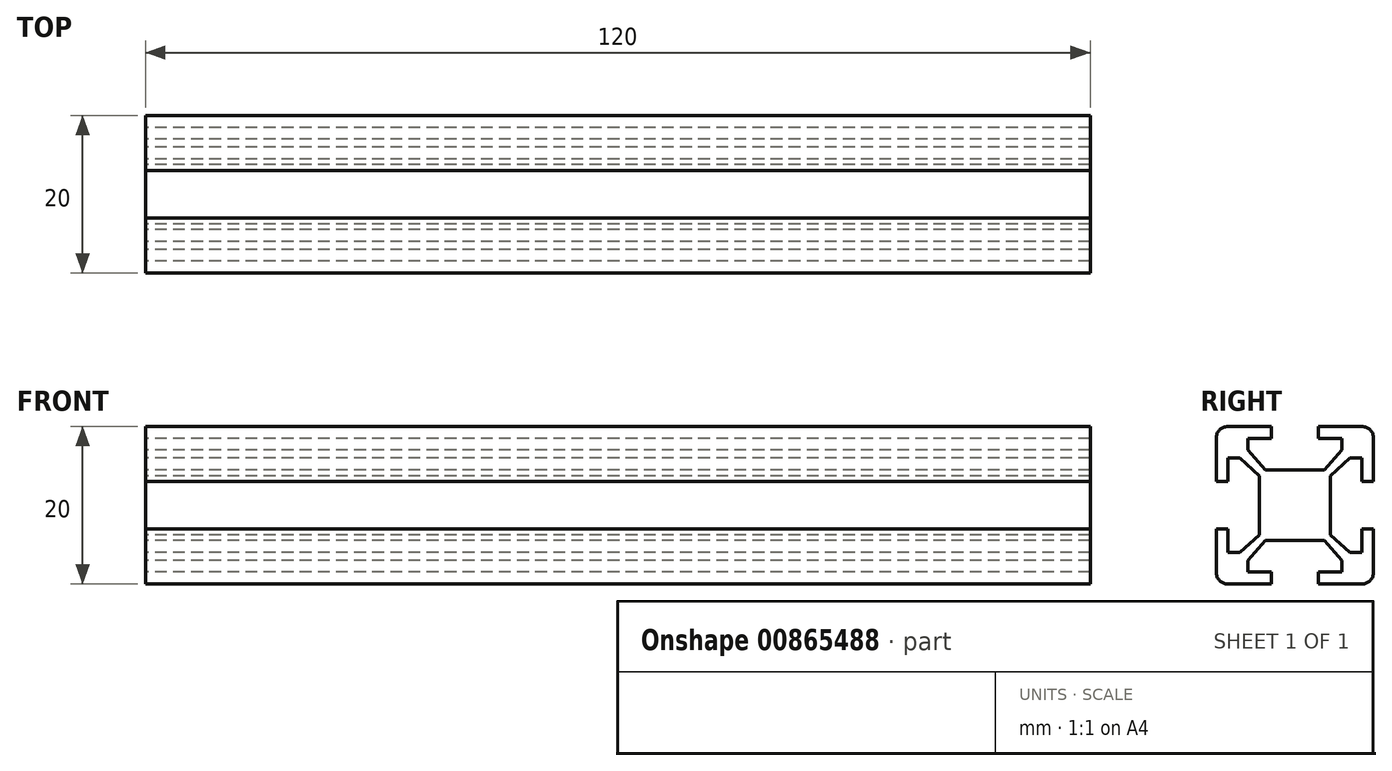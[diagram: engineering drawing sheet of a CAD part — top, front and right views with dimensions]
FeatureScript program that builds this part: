
annotation { "Feature Type Name" : "Feature", "Feature Type Description" : "" }
export const myFeature = defineFeature(function(context is Context, id is Id, definition is map)
    precondition{}
    {
        {
            var Q0;
            Q0=qCreatedBy(makeId("Right.planeOp"),FACE);
            var sketch = newSketch(context, id + "F0", { "sketchPlane" : qUnion([Q0])});
            skLineSegment(sketch, "E0.bottom", {"start": v(8.5, 10) * mm, "end": v(3, 10) * mm});
            skLineSegment(sketch, "E0.top", {"start": v(8.5, -10) * mm, "end": v(-8.5, -10) * mm});
            skLineSegment(sketch, "E0.left", {"start": v(10, 8.5) * mm, "end": v(10, 3) * mm});
            skLineSegment(sketch, "E0.right", {"start": v(-10, 8.5) * mm, "end": v(-10, 3) * mm});
            skPoint(sketch, "E0.middle", {"position": v(0, 0) * mm});
            skPoint(sketch, "E1.visualSharp", {"position": v(-10, 10) * mm});
            skArc(sketch, "E1.filletArc", {"start": v(-8.5, 10) * mm, "mid": v(-9.56, 9.56) * mm, "end": v(-10, 8.5) * mm});
            skPoint(sketch, "E2.visualSharp", {"position": v(10, 10) * mm});
            skArc(sketch, "E2.filletArc", {"start": v(10, 8.5) * mm, "mid": v(9.56, 9.56) * mm, "end": v(8.5, 10) * mm});
            skPoint(sketch, "E3.visualSharp", {"position": v(10, -10) * mm});
            skArc(sketch, "E3.filletArc", {"start": v(8.5, -10) * mm, "mid": v(9.56, -9.56) * mm, "end": v(10, -8.5) * mm});
            skPoint(sketch, "E4.visualSharp", {"position": v(-10, -10) * mm});
            skArc(sketch, "E4.filletArc", {"start": v(-10, -8.5) * mm, "mid": v(-9.56, -9.56) * mm, "end": v(-8.5, -10) * mm});
            skLineSegment(sketch, "E5", {"start": v(-3, 10) * mm, "end": v(-3, 8.5) * mm});
            skLineSegment(sketch, "E6", {"start": v(-3, 8.5) * mm, "end": v(-6, 8.5) * mm});
            skLineSegment(sketch, "E7", {"start": v(-6, 8.5) * mm, "end": v(-6, 7) * mm});
            skLineSegment(sketch, "E8", {"start": v(-6, 7) * mm, "end": v(-3.75, 4.5) * mm});
            skLineSegment(sketch, "E9", {"start": v(-3.75, 4.5) * mm, "end": v(0, 4.5) * mm});
            skLineSegment(sketch, "E10.MirrorCS", {"start": v(3, 10) * mm, "end": v(3, 8.5) * mm});
            skLineSegment(sketch, "E11.MirrorCS", {"start": v(3, 8.5) * mm, "end": v(6, 8.5) * mm});
            skLineSegment(sketch, "E12.MirrorCS", {"start": v(6, 8.5) * mm, "end": v(6, 7) * mm});
            skLineSegment(sketch, "E13.MirrorCS", {"start": v(6, 7) * mm, "end": v(3.75, 4.5) * mm});
            skLineSegment(sketch, "E14.MirrorCS", {"start": v(3.75, 4.5) * mm, "end": v(0, 4.5) * mm});
            skLineSegment(sketch, "E15.trimOffspring", {"start": v(-3, 10) * mm, "end": v(-8.5, 10) * mm});
            skLineSegment(sketch, "E16.1.0", {"start": v(-8.5, -3) * mm, "end": v(-8.5, -6) * mm});
            skLineSegment(sketch, "E16.1.1", {"start": v(-8.5, -6) * mm, "end": v(-7, -6) * mm});
            skLineSegment(sketch, "E16.1.2", {"start": v(-7, -6) * mm, "end": v(-4.5, -3.75) * mm});
            skLineSegment(sketch, "E16.1.3", {"start": v(-4.5, -3.75) * mm, "end": v(-4.5, 0) * mm});
            skLineSegment(sketch, "E16.1.4", {"start": v(-4.5, 3.75) * mm, "end": v(-4.5, 0) * mm});
            skLineSegment(sketch, "E16.1.5", {"start": v(-7, 6) * mm, "end": v(-4.5, 3.75) * mm});
            skLineSegment(sketch, "E16.1.6", {"start": v(-8.5, 6) * mm, "end": v(-7, 6) * mm});
            skLineSegment(sketch, "E16.1.7", {"start": v(-8.5, 3) * mm, "end": v(-8.5, 6) * mm});
            skLineSegment(sketch, "E16.1.8", {"start": v(-10, 3) * mm, "end": v(-8.5, 3) * mm});
            skLineSegment(sketch, "E16.1.9", {"start": v(-10, -3) * mm, "end": v(-8.5, -3) * mm});
            skLineSegment(sketch, "E16.2.0", {"start": v(3, -8.5) * mm, "end": v(6, -8.5) * mm});
            skLineSegment(sketch, "E16.2.1", {"start": v(6, -8.5) * mm, "end": v(6, -7) * mm});
            skLineSegment(sketch, "E16.2.2", {"start": v(6, -7) * mm, "end": v(3.75, -4.5) * mm});
            skLineSegment(sketch, "E16.2.3", {"start": v(3.75, -4.5) * mm, "end": v(0, -4.5) * mm});
            skLineSegment(sketch, "E16.2.4", {"start": v(-3.75, -4.5) * mm, "end": v(0, -4.5) * mm});
            skLineSegment(sketch, "E16.2.5", {"start": v(-6, -7) * mm, "end": v(-3.75, -4.5) * mm});
            skLineSegment(sketch, "E16.2.6", {"start": v(-6, -8.5) * mm, "end": v(-6, -7) * mm});
            skLineSegment(sketch, "E16.2.7", {"start": v(-3, -8.5) * mm, "end": v(-6, -8.5) * mm});
            skLineSegment(sketch, "E16.2.8", {"start": v(-3, -10) * mm, "end": v(-3, -8.5) * mm});
            skLineSegment(sketch, "E16.2.9", {"start": v(3, -10) * mm, "end": v(3, -8.5) * mm});
            skLineSegment(sketch, "E16.3.0", {"start": v(8.5, 3) * mm, "end": v(8.5, 6) * mm});
            skLineSegment(sketch, "E16.3.1", {"start": v(8.5, 6) * mm, "end": v(7, 6) * mm});
            skLineSegment(sketch, "E16.3.2", {"start": v(7, 6) * mm, "end": v(4.5, 3.75) * mm});
            skLineSegment(sketch, "E16.3.3", {"start": v(4.5, 3.75) * mm, "end": v(4.5, 0) * mm});
            skLineSegment(sketch, "E16.3.4", {"start": v(4.5, -3.75) * mm, "end": v(4.5, 0) * mm});
            skLineSegment(sketch, "E16.3.5", {"start": v(7, -6) * mm, "end": v(4.5, -3.75) * mm});
            skLineSegment(sketch, "E16.3.6", {"start": v(8.5, -6) * mm, "end": v(7, -6) * mm});
            skLineSegment(sketch, "E16.3.7", {"start": v(8.5, -3) * mm, "end": v(8.5, -6) * mm});
            skLineSegment(sketch, "E16.3.8", {"start": v(10, -3) * mm, "end": v(8.5, -3) * mm});
            skLineSegment(sketch, "E16.3.9", {"start": v(10, 3) * mm, "end": v(8.5, 3) * mm});
            skLineSegment(sketch, "E17.trimOffspring", {"start": v(-10, -3) * mm, "end": v(-10, -8.5) * mm});
            skLineSegment(sketch, "E18.trimOffspring", {"start": v(10, -3) * mm, "end": v(10, -8.5) * mm});
            skSolve(sketch);
        }
        {
            var Q0;
            Q0=makeQuery(id+"F0.imprint","IMPRINT",FACE,{"disambiguationData":[TD([[makeQuery(id+"F0.imprint","IMPRINT",EDGE,{"derivedFrom":sQuery(id+"F0.wireOp",EDGE,"E0.bottom")}),1.0]])]});
            extrude(context, id + "F1", {"entities" : qUnion([Q0]), "depth" : 120 * mm, "offsetDistance" : 25 * mm});
        }
    });
